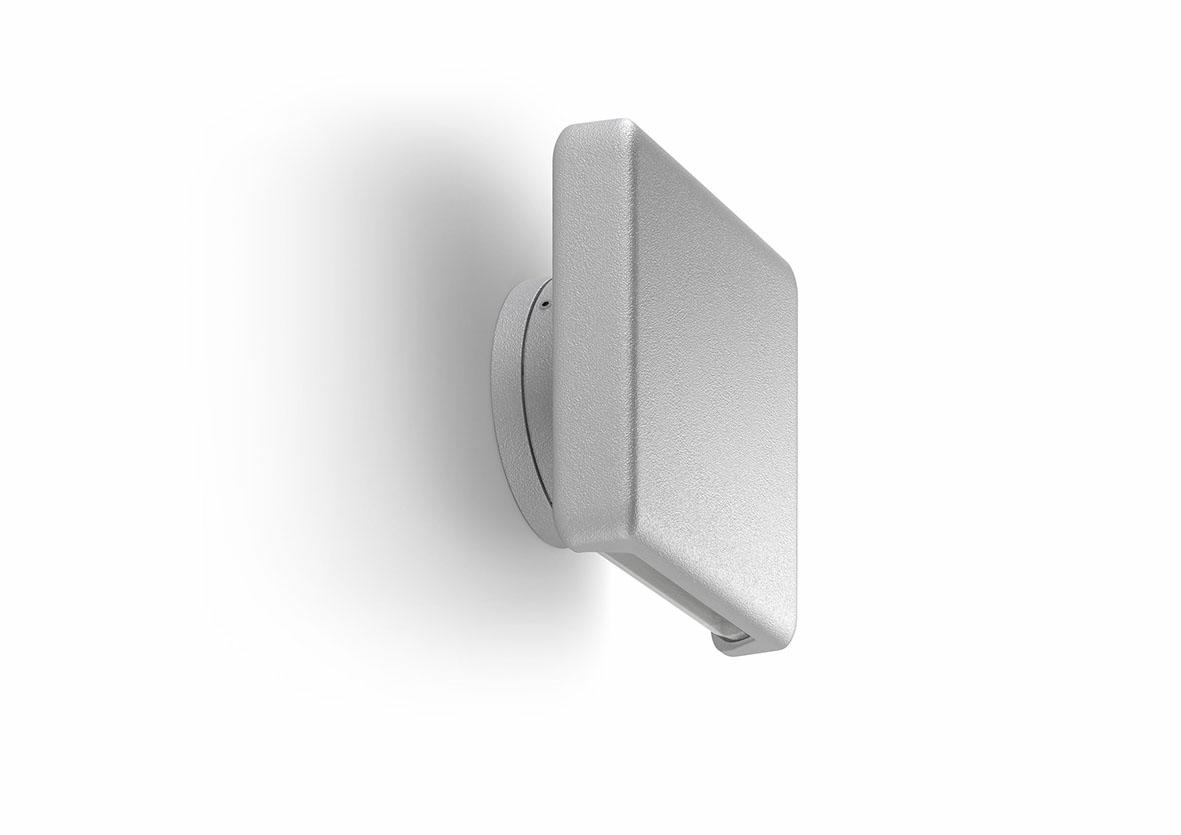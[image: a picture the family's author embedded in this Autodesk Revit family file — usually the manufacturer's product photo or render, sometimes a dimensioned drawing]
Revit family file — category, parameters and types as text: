
# Revit family: Platek_Blend Applique_2_Openings
name_source: partatom
category: Apparecchi per illuminazione
revit_build: Autodesk Revit 2017 (Build: 20160225_1515(x64)
units: mm (PartAtom-declared; Revit-internal decimal feet)

## family parameters
Basato su piano di lavoro = No
Condiviso = No
Punto di calcolo locali = No
Quota connettore circolare = Usa diametro
Sempre verticale = Sì
Sorgente d'illuminazione = No
Taglio con vuoti quando caricato = No
Tipo di parte = Normale

## types (1)
- 1610217_19W_LED_3000K
    Aluminium = PLK_Aluminium
    Angolo di inclinazione = 0.00°
    Body = PLK_06_Grey
    CRI = >80
    Carico apparente = 0 VA
    Codice assieme = 1610217.02(White);  1610217.06(Grey);  1610217.01(Black);  1610217.08(Anthracite);  1610217.01(Black);  1610217.07(Corten);  1610217.09(Bronze)
    Colour Temperature = 3000 K
    Commenti sul tipo = Facades, Wall
    Descrizione = Outdoor Lighting, Wall mounted
    Diffuse Type = Transparent Glass
    Dimmable = On request
    Energy Efficiency Rating = A/A+/A++
    Frequency = 50/60 Hz
    IK Rating = IK 05
    IP Rating = IP65
    Immagine tipo = blend_applique_1-2_finestre_1.jpg
    Insulation Class = 1
    LED Protection = Surge protection included
    Lampada = 2 LED Lamp
    Light Source = PLK_Light Source
    Luminaire Luminous Flux = 1395 lm
    Luminaire Luminous Intensity = 1073 cd
    Luminaire Wattage = 19 W
    Manufacturer Comment = 2 Openings
    Modello = Blend Applique 2 Openings
    Mounting Type = Wall
    Nota chiave = Other LED colors available on request
    PLATEK Article Code = 1610217
    Power Supply Unit = Included
    Product Dimension = L160mm x L160mm x 71,5mm
    Product Documentation Link = http://www.platek.eu
    Product Page URL = http://www.platek.eu
    Produttore = PLATEK SRL
    Supply Voltage = 230 V
    Supply Voltage Max = 240 V
    Supply Voltage Min = 220 V
    URL = www.platek.eu

## geometry (parser evidence)
native form markers: Blend x6
no freeform markers — native parametric forms only
